# Revit family: Genie_ElectricScissorLift_(GS-1432m)a
name_source: partatom
category: Site
units: mm (PartAtom-declared; Revit-internal decimal feet)

## family parameters
Always vertical = Yes
Cut with Voids When Loaded = No
OmniClass Number = 23.50.05.14.11
OmniClass Title = Scissors Lifts
Part Type = Normal
Round Connector Dimension = Use Diameter
Shared = No
Work Plane-Based = No

## types (1)
- GS-1432m Electric Scissor Lift
    Assembly Code = E1030900
    AssetType = Moveable
    BIMObjectName = Genie_ElectricScissorLift_(GS-1432m)
    Blue = Steel, Paint Finish, Blue, Genie
    ClassificationName = Uniclass2015
    ClassificationValue = TE_30_30_60_60
    Color = Blue
    Cost = 0 $
    Description = Designed for low-level access on sensitive flooring and space restricted applications, the Genie® GS™-1432m E-Drive scissor lift delivers quality and durability while improving total cost of ownership and productivity. It is equipped with an efficient, all-electric AC drive system that offers unmatched productivity for getting around indoor and outdoor jobsites in a compact, lightweight and versatile package.

Overview:

Micro-size ideal for low-level installation and maintenance jobs in tight spaces 
Zero inside turning radius
Powerful AC electric drive motors for unmatched driving performance and industry-leading runtime per battery charge
Low weight (1,984 lb / 900 kg), ideal for work on sensitive floors
500 lb (227 kg ) max lift capacity indoors and outdoors
Fits through a doorway with fixed rails
2 person max. platform occupancy indoors and 1 person outdoors
User-friendly Smart Link™ dual-zone controls for indoor and outdoor use
    DocumentationCertificates = https://www.bimstore.co
    DocumentationInstallationGuide = https://www.bimstore.co
    DocumentationLiterature = https://www.bimstore.co
    DocumentationMaintenance = https://www.bimstore.co
    DocumentationTechnical = https://www.bimstore.co
    DurationUnit = Years
    ExpectedLife = 0
    Grey = Steel, Paint Finish, Grey, Genie
    IfcExportAs = IfcTransportElement
    IfcExportType = IfcTransportElementType
    Keynote = X
    Manufacturer = Genie
    ManufacturerName = Genie
    Model = GS-1432m Electric Scissor Lift
    ModelNumber = GS-1432m
    ModelReference = Electric Scissor Lift
    NBSDescription = Scissor lifts
    NBSObjectName = Genie - Scissor lifts
    NominalDepth = 0 mm  [stored 0 ft]
    NominalHeight = 0 mm  [stored 0 ft]
    NominalLength = 0 mm  [stored 0 ft]
    ProductionYear = 2024
    SpareParts = https://www.genielift.com
    Type Comments = GS-1432m Electric Scissor Lift
    TypeName = GS-1432m Electric Scissor Lift
    URL = https://www.genielift.com
    WarrantyDurationLabor = 0
    WarrantyDurationParts = 0
    WarrantyDurationUnit = Years
    WarrantyGuarantorLabor = https://www.genielift.com
    WarrantyGuarantorParts = https://www.genielift.com
    _BSBibleVersion = 17
    _BimSpecGuid = 0
    _CurrentRevision = 1
    _DistributedBy = https://www.bimstore.co
    _ObjectUserGuide = https://www.bimstore.co

note: [stored X ft] marks values corroborated as IEEE doubles in the binary element streams (Revit-internal decimal feet)

## geometry (parser evidence)
native form markers: Sweep x16
no freeform markers — native parametric forms only
